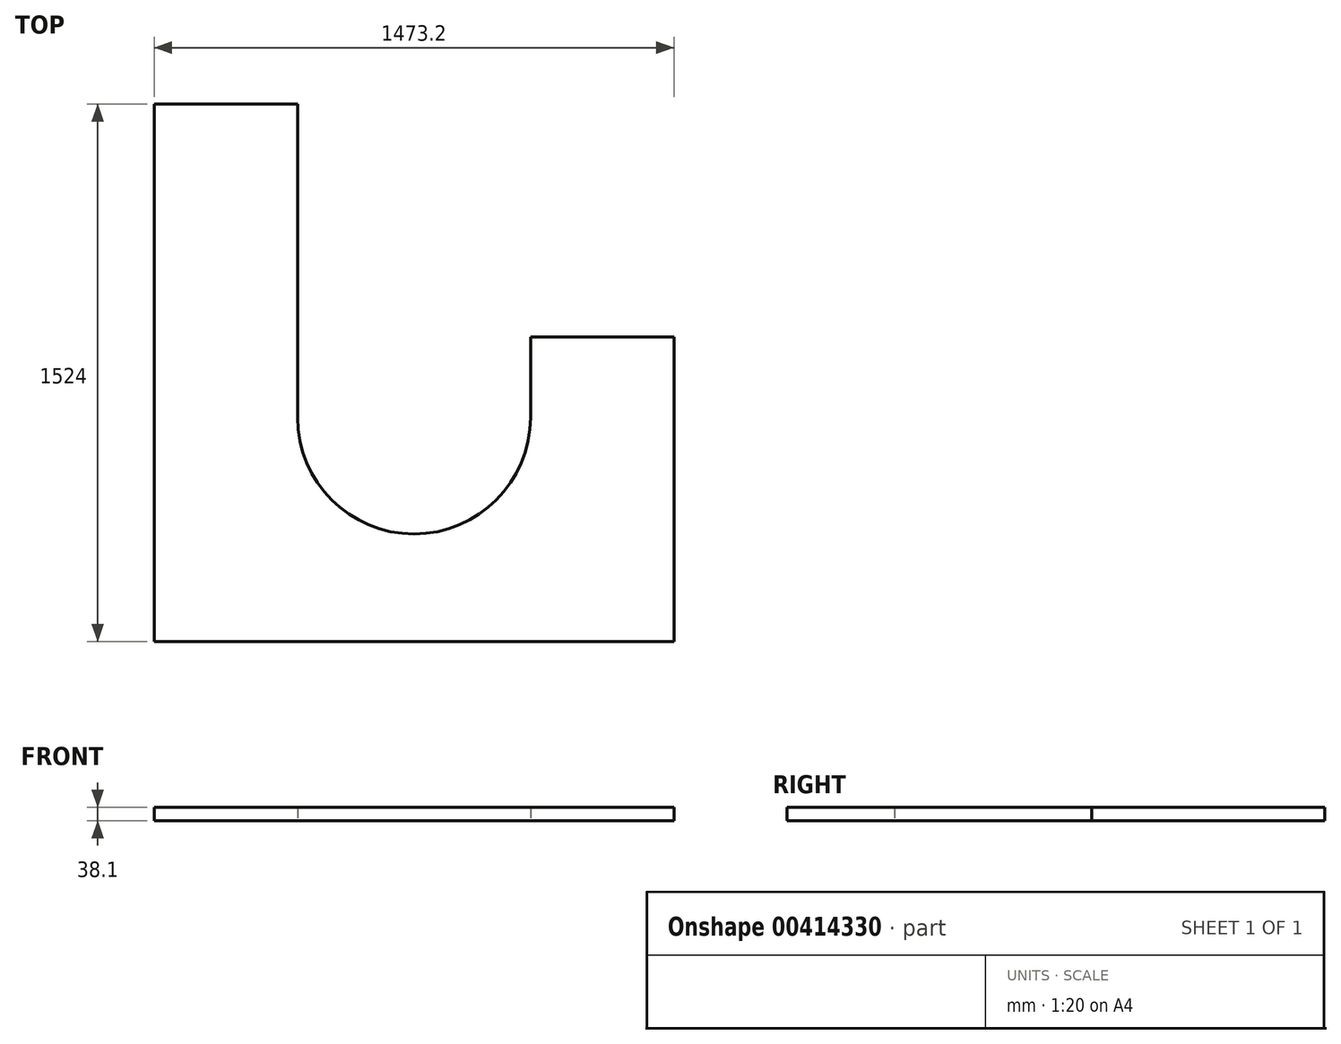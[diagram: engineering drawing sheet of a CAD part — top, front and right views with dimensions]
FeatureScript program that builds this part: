
annotation { "Feature Type Name" : "Feature", "Feature Type Description" : "" }
export const myFeature = defineFeature(function(context is Context, id is Id, definition is map)
    precondition{}
    {
        {
            var Q0;
            Q0=qCreatedBy(makeId("Top.planeOp"),FACE);
            var sketch = newSketch(context, id + "F0", { "sketchPlane" : qUnion([Q0])});
            skLineSegment(sketch, "E0", {"start": v(0, 0) * mm, "end": v(0, -330.2) * mm});
            skLineSegment(sketch, "E1", {"start": v(-330.2, 0) * mm, "end": v(-330.2, 889) * mm});
            skArc(sketch, "E2", {"start": v(-330.2, 0) * mm, "mid": v(0, -330.2) * mm, "end": v(330.2, 0) * mm});
            skLineSegment(sketch, "E3", {"start": v(-330.2, 889) * mm, "end": v(-736.6, 889) * mm});
            skLineSegment(sketch, "E4", {"start": v(-736.6, 889) * mm, "end": v(-736.6, -635) * mm});
            skLineSegment(sketch, "E5", {"start": v(-736.6, -635) * mm, "end": v(736.6, -635) * mm});
            skLineSegment(sketch, "E6", {"start": v(330.2, 0) * mm, "end": v(330.2, 228.6) * mm});
            skLineSegment(sketch, "E7", {"start": v(330.2, 228.6) * mm, "end": v(736.6, 228.6) * mm});
            skLineSegment(sketch, "E8", {"start": v(736.6, -635) * mm, "end": v(736.6, 228.6) * mm});
            skSolve(sketch);
        }
        {
            var Q0;
            {var subQ3=sQuery(id+"F0.wireOp",EDGE,"E1");Q0=makeQuery(id+"F0.imprint","IMPRINT",FACE,{"disambiguationData":[TD([[makeQuery(id+"F0.imprint","IMPRINT",EDGE,{"derivedFrom":subQ3}),1.0]])]});}
            extrude(context, id + "F1", {"entities" : qUnion([Q0]), "depth" : 38.1 * mm});
        }
    });
